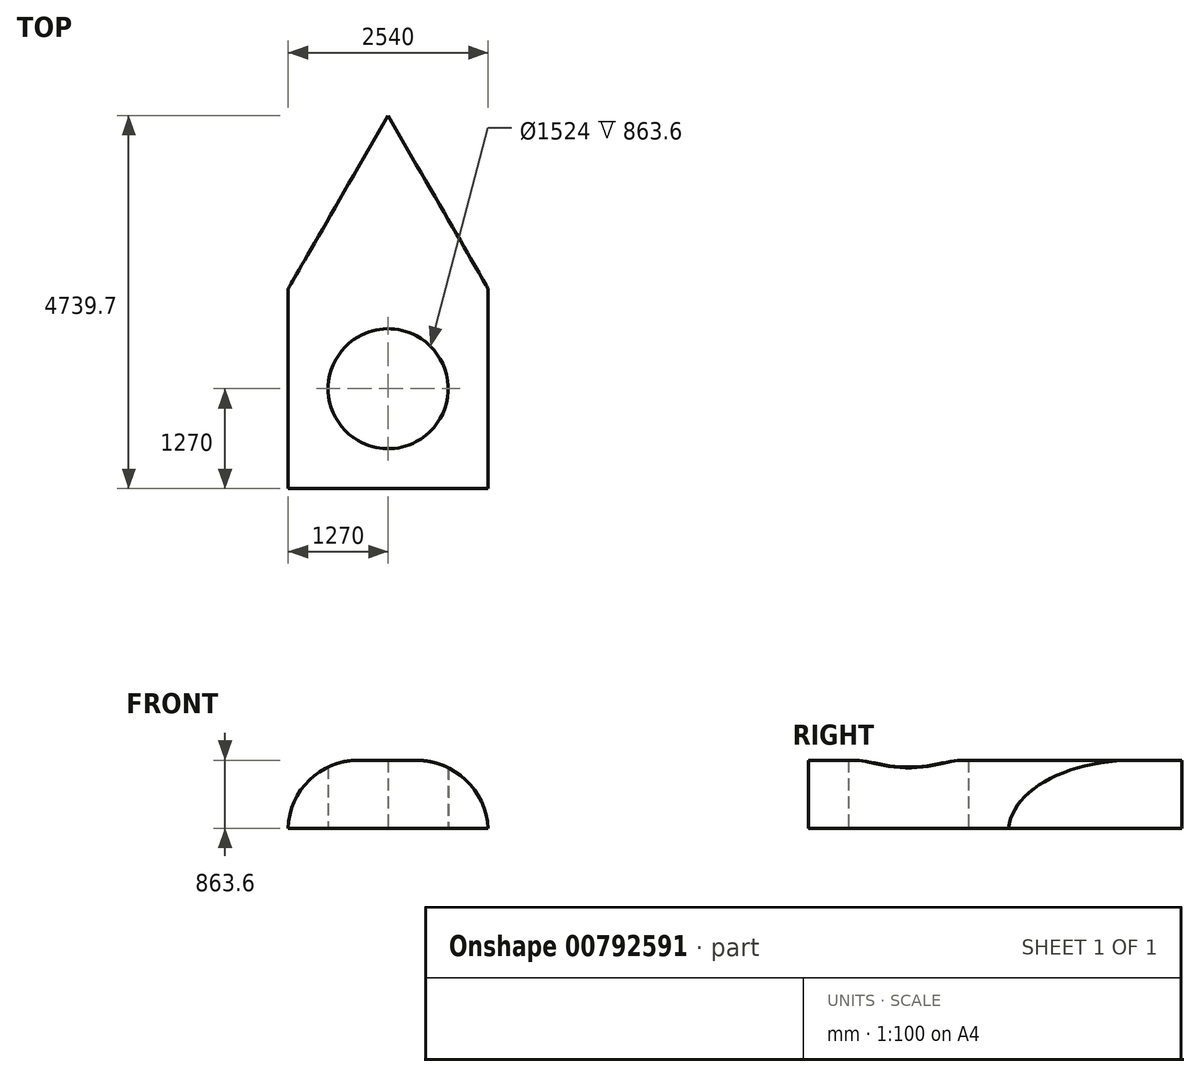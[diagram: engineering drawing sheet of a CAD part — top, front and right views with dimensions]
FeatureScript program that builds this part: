
annotation { "Feature Type Name" : "Feature", "Feature Type Description" : "" }
export const myFeature = defineFeature(function(context is Context, id is Id, definition is map)
    precondition{}
    {
        {
            var Q0;
            Q0=qCreatedBy(makeId("Top.planeOp"),FACE);
            var sketch = newSketch(context, id + "F0", { "sketchPlane" : qUnion([Q0])});
            skLineSegment(sketch, "E0.bottom", {"start": v(-1270, 1270) * mm, "end": v(1270, 1270) * mm});
            skLineSegment(sketch, "E0.top", {"start": v(-1270, -1270) * mm, "end": v(1270, -1270) * mm});
            skLineSegment(sketch, "E0.left", {"start": v(-1270, 1270) * mm, "end": v(-1270, -1270) * mm});
            skLineSegment(sketch, "E0.right", {"start": v(1270, 1270) * mm, "end": v(1270, -1270) * mm});
            skCircle(sketch, "E1", {"center": v(0, 0) * mm, "radius": 762 * mm});
            skLineSegment(sketch, "E2", {"start": v(-1270, 1270) * mm, "end": v(0, 3469.7) * mm});
            skLineSegment(sketch, "E3", {"start": v(0, 3469.7) * mm, "end": v(1270, 1270) * mm});
            skLineSegment(sketch, "E4", {"start": v(-1270, 1270) * mm, "end": v(1270, -1270) * mm, "construction": true});
            skSolve(sketch);
        }
        {
            var Q0;
            Q0=makeQuery(id+"F0.imprint","IMPRINT",FACE,{"disambiguationData":[TD([[makeQuery(id+"F0.imprint","IMPRINT",EDGE,{"derivedFrom":sQuery(id+"F0.wireOp",EDGE,"E0.bottom")}),-1.0]])]});
            var Q1;
            Q1=makeQuery(id+"F0.imprint","IMPRINT",FACE,{"disambiguationData":[TD([[makeQuery(id+"F0.imprint","IMPRINT",EDGE,{"derivedFrom":sQuery(id+"F0.wireOp",EDGE,"E0.bottom")}),1.0]])]});
            extrude(context, id + "F1", {"entities" : qUnion([Q0, Q1]), "depth" : 863.6 * mm, "offsetDistance" : 25.4 * mm});
        }
        {
            var Q0;
            Q0=makeQuery(id+"F1.opExtrude","CAP_EDGE",EDGE,{"disambiguationData":[OSD([sQuery(id+"F0.wireOp",EDGE,"E0.left")])],"isStart":false});
            fillet(context, id + "F2", {"entities" : qUnion([Q0]), "radius" : 889.15 * mm, "tangentPropagation" : true, "allowEdgeOverflow" : false});
        }
        {
            var Q0;
            Q0=makeQuery(id+"F1.opExtrude","CAP_EDGE",EDGE,{"disambiguationData":[OSD([sQuery(id+"F0.wireOp",EDGE,"E0.right")])],"isStart":false});
            fillet(context, id + "F3", {"entities" : qUnion([Q0]), "radius" : 913.68 * mm, "tangentPropagation" : true, "allowEdgeOverflow" : false});
        }
        {
            var Q0;
            Q0=makeQuery(id+"F1.opExtrude","CAP_FACE",FACE,{"disambiguationData":[OSD([sQuery(id+"F0.wireOp",EDGE,"E0.top"),sQuery(id+"F0.wireOp",EDGE,"E0.left"),sQuery(id+"F0.wireOp",EDGE,"E0.right"),sQuery(id+"F0.wireOp",EDGE,"E1"),sQuery(id+"F0.wireOp",EDGE,"E2"),sQuery(id+"F0.wireOp",EDGE,"E3")])],"isStart":true});
            shell(context, id + "F4", {"entities" : qUnion([Q0]), "thickness" : 2.54 * mm});
        }
    });
